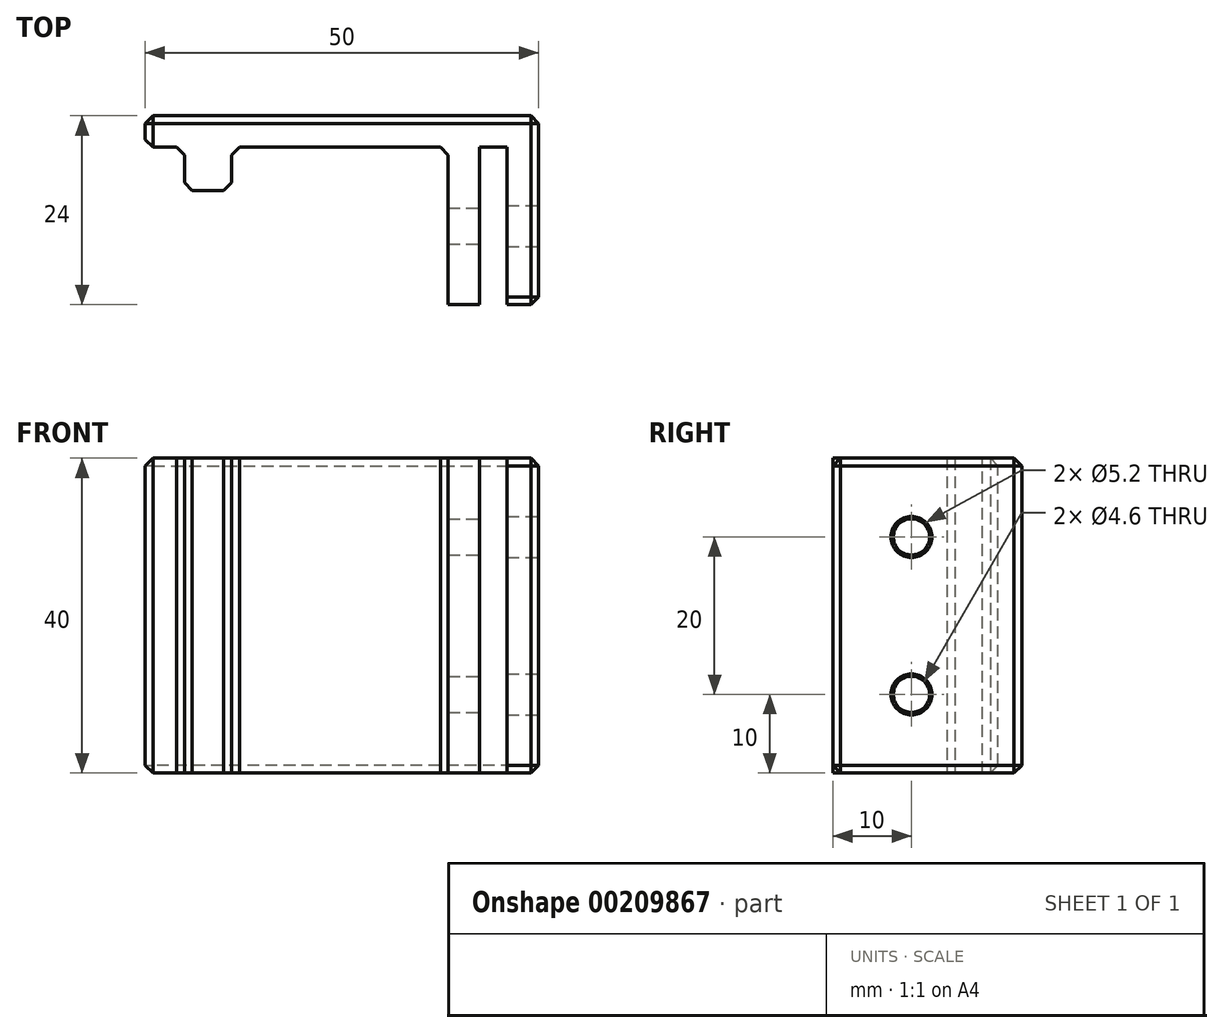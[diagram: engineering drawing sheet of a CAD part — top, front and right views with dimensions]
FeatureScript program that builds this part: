
annotation { "Feature Type Name" : "Feature", "Feature Type Description" : "" }
export const myFeature = defineFeature(function(context is Context, id is Id, definition is map)
    precondition{}
    {
        {
            var Q0;
            Q0=qCreatedBy(makeId("Top.planeOp"),FACE);
            var sketch = newSketch(context, id + "F0", { "sketchPlane" : qUnion([Q0])});
            skLineSegment(sketch, "E0.bottom", {"start": v(-58.82, 21) * mm, "end": v(-8.82, 21) * mm});
            skLineSegment(sketch, "E0.top", {"start": v(-58.82, 17) * mm, "end": v(-8.82, 17) * mm});
            skLineSegment(sketch, "E0.left", {"start": v(-58.82, 21) * mm, "end": v(-58.82, 17) * mm});
            skLineSegment(sketch, "E0.right", {"start": v(-8.82, 21) * mm, "end": v(-8.82, 17) * mm});
            skLineSegment(sketch, "E1.bottom", {"start": v(-12.82, 17) * mm, "end": v(-8.82, 17) * mm});
            skLineSegment(sketch, "E1.top", {"start": v(-12.82, -3) * mm, "end": v(-8.82, -3) * mm});
            skLineSegment(sketch, "E1.left", {"start": v(-12.82, 17) * mm, "end": v(-12.82, -3) * mm});
            skLineSegment(sketch, "E1.right", {"start": v(-8.82, 17) * mm, "end": v(-8.82, -3) * mm});
            skLineSegment(sketch, "E2.bottom", {"start": v(-53.82, 17) * mm, "end": v(-47.82, 17) * mm});
            skLineSegment(sketch, "E2.top", {"start": v(-53.82, 11.5) * mm, "end": v(-47.82, 11.5) * mm});
            skLineSegment(sketch, "E2.left", {"start": v(-53.82, 17) * mm, "end": v(-53.82, 11.5) * mm});
            skLineSegment(sketch, "E2.right", {"start": v(-47.82, 17) * mm, "end": v(-47.82, 11.5) * mm});
            skLineSegment(sketch, "E3.bottom", {"start": v(-20.32, 17) * mm, "end": v(-16.32, 17) * mm});
            skLineSegment(sketch, "E3.top", {"start": v(-20.32, -3) * mm, "end": v(-16.32, -3) * mm});
            skLineSegment(sketch, "E3.left", {"start": v(-20.32, 17) * mm, "end": v(-20.32, -3) * mm});
            skLineSegment(sketch, "E3.right", {"start": v(-16.32, 17) * mm, "end": v(-16.32, -3) * mm});
            skSolve(sketch);
        }
        {
            var Q0;
            Q0 = qSketchRegion(id + "F0", true);
            extrude(context, id + "F1", {"entities" : qUnion([Q0]), "depth" : 40 * mm});
        }
        {
            var Q0;
            Q0=makeQuery(id+"F1.opExtrude","SWEPT_EDGE",EDGE,{"disambiguationData":[OSD([sQuery(id+"F0.wireOp",EDGE,"E0.top"),sQuery(id+"F0.wireOp",EDGE,"E2.bottom"),sQuery(id+"F0.wireOp",EDGE,"E2.right")])]});
            var Q1;
            Q1=makeQuery(id+"F1.opExtrude","SWEPT_EDGE",EDGE,{"disambiguationData":[OSD([sQuery(id+"F0.wireOp",EDGE,"E0.top"),sQuery(id+"F0.wireOp",EDGE,"E2.bottom"),sQuery(id+"F0.wireOp",EDGE,"E2.left")])]});
            var Q2;
            Q2=makeQuery(id+"F1.opExtrude","SWEPT_EDGE",EDGE,{"disambiguationData":[OSD([sQuery(id+"F0.wireOp",EDGE,"E2.top"),sQuery(id+"F0.wireOp",EDGE,"E2.left")])]});
            var Q3;
            Q3=makeQuery(id+"F1.opExtrude","SWEPT_EDGE",EDGE,{"disambiguationData":[OSD([sQuery(id+"F0.wireOp",EDGE,"E0.top"),sQuery(id+"F0.wireOp",EDGE,"E0.left")])]});
            var Q4;
            Q4=makeQuery(id+"F1.opExtrude","SWEPT_EDGE",EDGE,{"disambiguationData":[OSD([sQuery(id+"F0.wireOp",EDGE,"E0.bottom"),sQuery(id+"F0.wireOp",EDGE,"E0.left")])]});
            var Q5;
            Q5=makeQuery(id+"F1.opExtrude","SWEPT_EDGE",EDGE,{"disambiguationData":[OSD([sQuery(id+"F0.wireOp",EDGE,"E0.bottom"),sQuery(id+"F0.wireOp",EDGE,"E0.right")])]});
            var Q6;
            Q6=makeQuery(id+"F1.opExtrude","SWEPT_EDGE",EDGE,{"disambiguationData":[OSD([sQuery(id+"F0.wireOp",EDGE,"E1.top"),sQuery(id+"F0.wireOp",EDGE,"E1.right")])]});
            var Q7;
            Q7=makeQuery(id+"F1.opExtrude","CAP_EDGE",EDGE,{"disambiguationData":[OSD([sQuery(id+"F0.wireOp",EDGE,"E0.bottom")])],"isStart":false});
            var Q8;
            Q8=makeQuery(id+"F1.opExtrude","CAP_EDGE",EDGE,{"disambiguationData":[OSD([sQuery(id+"F0.wireOp",EDGE,"E0.bottom")])],"isStart":true});
            var Q9;
            Q9=makeQuery(id+"F1.opExtrude","SWEPT_EDGE",EDGE,{"disambiguationData":[OSD([sQuery(id+"F0.wireOp",EDGE,"E0.top"),sQuery(id+"F0.wireOp",EDGE,"E3.bottom"),sQuery(id+"F0.wireOp",EDGE,"E3.left")])]});
            var Q10;
            Q10=makeQuery(id+"F1.opExtrude","CAP_EDGE",EDGE,{"disambiguationData":[OSD([sQuery(id+"F0.wireOp",EDGE,"E0.right"),sQuery(id+"F0.wireOp",EDGE,"E1.right")])],"isStart":false});
            var Q11;
            Q11=makeQuery(id+"F1.opExtrude","CAP_EDGE",EDGE,{"disambiguationData":[OSD([sQuery(id+"F0.wireOp",EDGE,"E0.right"),sQuery(id+"F0.wireOp",EDGE,"E1.right")])],"isStart":true});
            var Q12;
            Q12=makeQuery(id+"F1.opExtrude","CAP_EDGE",EDGE,{"disambiguationData":[OSD([sQuery(id+"F0.wireOp",EDGE,"E0.left")])],"isStart":false});
            var Q13;
            Q13=makeQuery(id+"F1.opExtrude","CAP_EDGE",EDGE,{"disambiguationData":[OSD([sQuery(id+"F0.wireOp",EDGE,"E0.left")])],"isStart":true});
            var Q14;
            Q14=makeQuery(id+"F1.opExtrude","SWEPT_EDGE",EDGE,{"disambiguationData":[OSD([sQuery(id+"F0.wireOp",EDGE,"E2.top"),sQuery(id+"F0.wireOp",EDGE,"E2.right")])]});
            var Q15;
            Q15=makeQuery(id+"F1.opExtrude","CAP_EDGE",EDGE,{"disambiguationData":[OSD([sQuery(id+"F0.wireOp",EDGE,"E1.top")])],"isStart":true});
            var Q16;
            Q16=makeQuery(id+"F1.opExtrude","CAP_EDGE",EDGE,{"disambiguationData":[OSD([sQuery(id+"F0.wireOp",EDGE,"E1.top")])],"isStart":false});
            chamfer(context, id + "F2", {"entities" : qUnion([Q0, Q1, Q2, Q3, Q4, Q5, Q6, Q7, Q8, Q9, Q10, Q11, Q12, Q13, Q14, Q15, Q16]), "width" : 1 * mm, "tangentPropagation" : true});
        }
        {
            var Q0;
            Q0=makeQuery(id+"F1.opExtrude","SWEPT_FACE",FACE,{"disambiguationData":[OSD([sQuery(id+"F0.wireOp",EDGE,"E0.right"),sQuery(id+"F0.wireOp",EDGE,"E1.right")])]});
            var sketch = newSketch(context, id + "F3", { "sketchPlane" : qUnion([Q0])});
            skPoint(sketch, "E4", {"position": v(7, 10) * mm});
            skPoint(sketch, "E5", {"position": v(7, 30) * mm});
            skSolve(sketch);
        }
        {
            var Q0;
            Q0=sQuery(id+"F3.wireOp",VERTEX,"E4");
            var Q1;
            Q1=sQuery(id+"F3.wireOp",VERTEX,"E5");
            var Q2;
            Q2=makeQuery(id+"F1.opExtrude","SWEPT_BODY",BODY,{"disambiguationData":[OSD([sQuery(id+"F0.wireOp",EDGE,"E0.bottom"),sQuery(id+"F0.wireOp",EDGE,"E0.top"),sQuery(id+"F0.wireOp",EDGE,"E0.left"),sQuery(id+"F0.wireOp",EDGE,"E0.right"),sQuery(id+"F0.wireOp",EDGE,"E1.top"),sQuery(id+"F0.wireOp",EDGE,"E1.left"),sQuery(id+"F0.wireOp",EDGE,"E1.right"),sQuery(id+"F0.wireOp",EDGE,"E2.top"),sQuery(id+"F0.wireOp",EDGE,"E2.left"),sQuery(id+"F0.wireOp",EDGE,"E2.right"),sQuery(id+"F0.wireOp",EDGE,"E3.top"),sQuery(id+"F0.wireOp",EDGE,"E3.left"),sQuery(id+"F0.wireOp",EDGE,"E3.right")])]});
            hole(context, id + "F4", {"style" : HoleStyle.C_BORE, "endStyle" : HoleEndStyle.BLIND, "holeDiameter" : 4.6 * mm, "cBoreDiameter" : 5.2 * mm, "cBoreDepth" : 6 * mm, "holeDepth" : 12 * mm, "tappedDepth" : 12 * mm, "tapClearance" : 3, "locations" : qUnion([Q0, Q1]), "scope" : qUnion([Q2])});
        }
    });
